# Revit family: Outdoor_Upper_Bottle_Filling_Station_Tri-Level_Pedestal-Elkay-LK4430BF1UEVG_BLU_BLK_GRY
name_source: partatom
category: Plumbing Fixtures
units: mm (PartAtom-declared; Revit-internal decimal feet)

## family parameters
Always vertical = Yes
Cut with Voids When Loaded = No
Maintain Annotation Orientation = No
OmniClass Number = 23.45.05.14.14
OmniClass Title = Sinks/Lavatories
Part Type = Normal
Room Calculation Point = No
Round Connector Dimension = Use Diameter
Shared = No
Work Plane-Based = Yes

## types (4) — shared parameters
Activation Method = Mechanical Button
Approx. Shipping Weight (lbs) = 215
Arm Height = 27 "
Assembly Code = D2010800
Base Thickness = 0.125 "
Default Elevation = 48 "
Description = Outdoor ezH2O®  Upper Bottle Filling Station Tri-Level Pedestal Non-Filtered Non-Refrigerated
Height = 64 "
Inlet Connection Size (inch) = 0.375 "
Length = 14 "
Manufacturer = Elkay (by Zurn Elkay Water Solutions)
Manufacturer Brand = Elkay Manufacturer Company
Outlet Connection Size(inch) = 1.5 "
Product Documentation Link = https://www.elkayfiles.com
Product Installation Sheet URL = https://www.elkayfiles.com
Product Page URL = https://www.elkay.com
Product Weight (lbs) = 182
Product data URL = https://bimobject.com
Repair Parts URL = https://www.elkayfiles.com
Secoundary Material = Finish-Elkay-Stainless Steel
URL = https://www.elkay.com
Width = 48 "
zero-valued in all types: CWFU, HWFU, WFU

## per-type parameters (varying)
| type | Main Material | Model |
| LK4430BF1UEVG (Upper Bottle Filling Station Tri-Level Pedestal Non-Filtered Non-Refrigerated Evergreen) | Finish-Elkay-Green | LK4430BF1UEVG |
| LK4430BF1UBLU (Upper Bottle Filling Station Tri-Level Pedestal Non-Filtered Non-Refrigerated Blue) | Finish- Elkay- Blue | LK4430BF1UBLU |
| LK4430BF1UBLK (Upper Bottle Filling Station Tri-Level Pedestal Non-Filtered Non-Refrigerated Black) | Finish-Elkay-Black | LK4430BF1UBLK |
| LK4430BF1UGRY (Upper Bottle Filling Station Tri-Level Pedestal Non-Filtered Non-Refrigerated Gray) | Finish-Elkay-Gray | LK4430BF1UGRY |

## geometry (parser evidence)
native form markers: Sweep x5
no freeform markers — native parametric forms only
